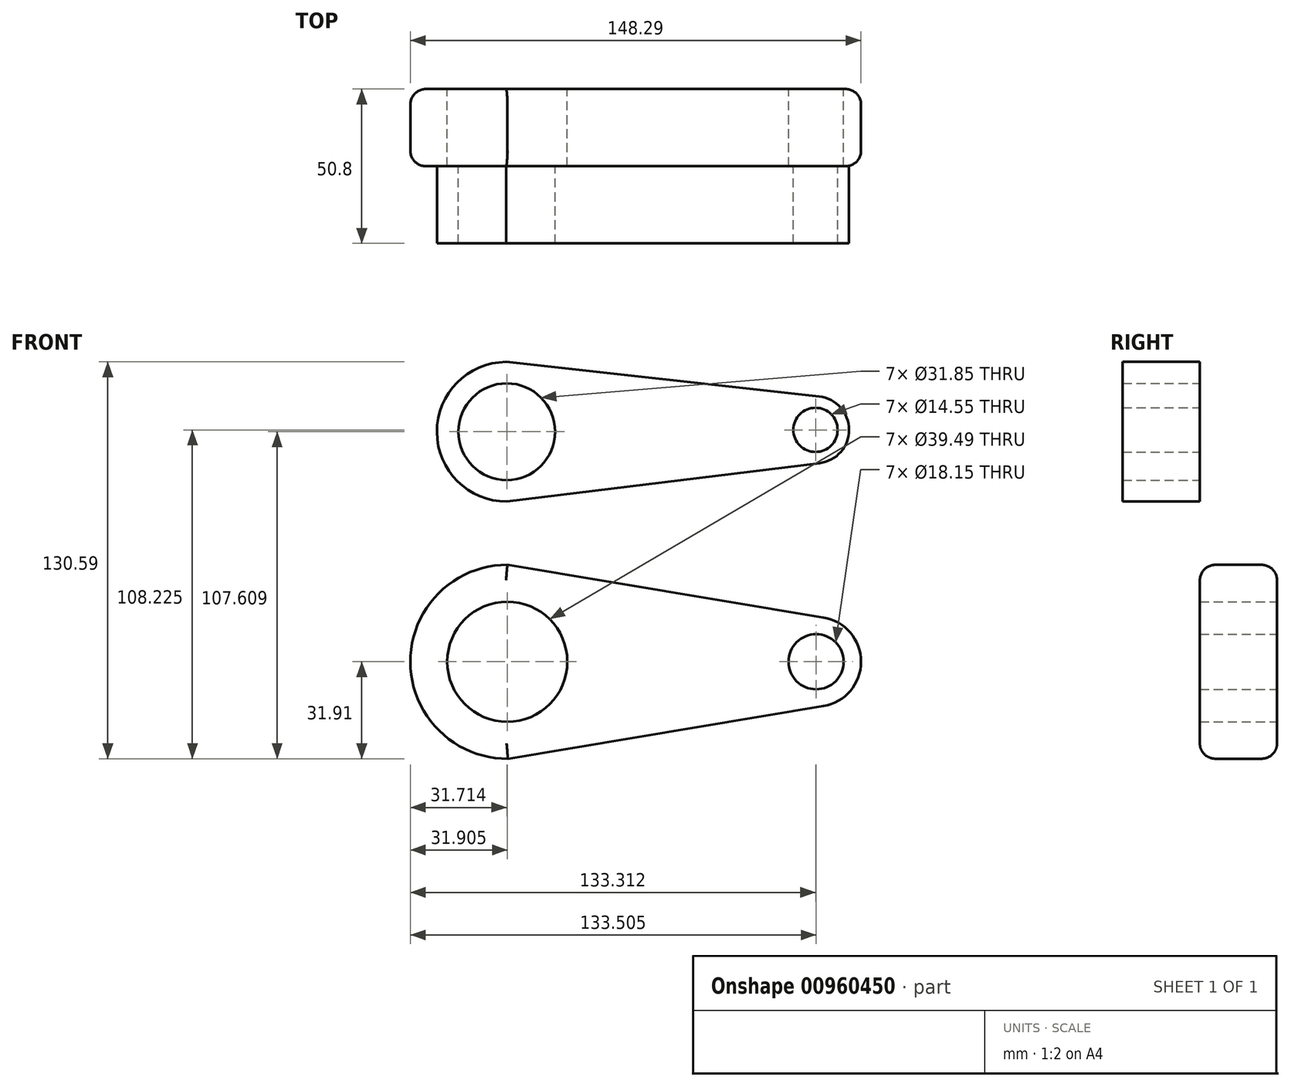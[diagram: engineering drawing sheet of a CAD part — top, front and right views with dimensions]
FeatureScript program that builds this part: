
annotation { "Feature Type Name" : "Feature", "Feature Type Description" : "" }
export const myFeature = defineFeature(function(context is Context, id is Id, definition is map)
    precondition{}
    {
        {
            var Q0;
            Q0=qCreatedBy(makeId("Front.planeOp"),FACE);
            var sketch = newSketch(context, id + "F0", { "sketchPlane" : qUnion([Q0])});
            skArc(sketch, "E0", {"start": v(-52.15, 31.9) * mm, "mid": v(-83.64, -5.16) * mm, "end": v(-41.98, -30.24) * mm});
            skArc(sketch, "E1", {"start": v(51.88, -14.58) * mm, "mid": v(64.23, 0) * mm, "end": v(51.87, 14.58) * mm});
            skLineSegment(sketch, "E2", {"start": v(-52.15, 31.9) * mm, "end": v(51.87, 14.58) * mm});
            skLineSegment(sketch, "E3", {"start": v(-51.96, -31.9) * mm, "end": v(51.88, -14.58) * mm});
            skCircle(sketch, "E4", {"center": v(-52.15, 0) * mm, "radius": 19.74 * mm});
            skCircle(sketch, "E5", {"center": v(49.45, 0) * mm, "radius": 9.08 * mm});
            skSolve(sketch);
        }
        {
            var Q0;
            {var subQ5=sQuery(id+"F0.wireOp",EDGE,"E1");Q0=makeQuery(id+"F0.imprint","IMPRINT",FACE,{"disambiguationData":[TD([[makeQuery(id+"F0.imprint","IMPRINT",EDGE,{"derivedFrom":subQ5}),1.0]])]});}
            extrude(context, id + "F1", {"entities" : qUnion([Q0]), "depth" : 25.4 * mm, "offsetDistance" : 25.4 * mm});
        }
        {
            var Q0;
            Q0=makeQuery(id+"F1.opExtrude","CAP_EDGE",EDGE,{"disambiguationData":[OSD([sQuery(id+"F0.wireOp",EDGE,"E3")])],"isStart":false});
            var Q1;
            Q1=makeQuery(id+"F1.opExtrude","CAP_EDGE",EDGE,{"disambiguationData":[OSD([sQuery(id+"F0.wireOp",EDGE,"E3")])],"isStart":true});
            var Q2;
            Q2=makeQuery(id+"F1.opExtrude","CAP_EDGE",EDGE,{"disambiguationData":[OSD([sQuery(id+"F0.wireOp",EDGE,"E0")])],"isStart":false});
            var Q3;
            Q3=makeQuery(id+"F1.opExtrude","CAP_EDGE",EDGE,{"disambiguationData":[OSD([sQuery(id+"F0.wireOp",EDGE,"E0")])],"isStart":true});
            fillet(context, id + "F2", {"entities" : qUnion([Q0, Q1, Q2, Q3]), "radius" : 5.08 * mm, "tangentPropagation" : true, "allowEdgeOverflow" : false});
        }
        {
            var Q0;
            Q0=makeQuery(id+"F1.opExtrude","CAP_FACE",FACE,{"disambiguationData":[OSD([sQuery(id+"F0.wireOp",EDGE,"E0"),sQuery(id+"F0.wireOp",EDGE,"E1"),sQuery(id+"F0.wireOp",EDGE,"E2"),sQuery(id+"F0.wireOp",EDGE,"E3"),sQuery(id+"F0.wireOp",EDGE,"E4"),sQuery(id+"F0.wireOp",EDGE,"E5")])],"isStart":false});
            var sketch = newSketch(context, id + "F3", { "sketchPlane" : qUnion([Q0])});
            skArc(sketch, "E6", {"start": v(-47.1, 98.07) * mm, "mid": v(-75.32, 75.54) * mm, "end": v(-46.79, 53.4) * mm});
            skArc(sketch, "E7", {"start": v(50.6, 65.36) * mm, "mid": v(60.29, 76.38) * mm, "end": v(50.46, 87.28) * mm});
            skLineSegment(sketch, "E8", {"start": v(-52.58, 98.68) * mm, "end": v(50.46, 87.28) * mm});
            skLineSegment(sketch, "E9", {"start": v(-52.35, 52.72) * mm, "end": v(50.6, 65.36) * mm});
            skCircle(sketch, "E10", {"center": v(-52.35, 75.7) * mm, "radius": 15.93 * mm});
            skCircle(sketch, "E11", {"center": v(49.25, 76.32) * mm, "radius": 7.28 * mm});
            skSolve(sketch);
        }
        {
            var Q0;
            {var subQ0=sQuery(id+"F3.wireOp",EDGE,"E8");var subQ1=sQuery(id+"F3.wireOp",EDGE,"E6");var subQ2=makeQuery(id+"F3.imprint","INTERSECT",VERTEX,{"disambiguationData":[OD(0.0)],"derivedFrom":[subQ1,subQ0]});Q0=makeQuery(id+"F3.imprint","IMPRINT",FACE,{"disambiguationData":[TD([[makeQuery(id+"F3.imprint","IMPRINT",EDGE,{"disambiguationData":[TD([[subQ2,-1.0]])],"derivedFrom":subQ1}),1.0]])]});}
            var Q1;
            {var subQ0=sQuery(id+"F3.wireOp",EDGE,"E9");var subQ1=sQuery(id+"F3.wireOp",EDGE,"E6");var subQ2=makeQuery(id+"F3.imprint","INTERSECT",VERTEX,{"disambiguationData":[OD(0.0)],"derivedFrom":[subQ1,subQ0]});Q1=makeQuery(id+"F3.imprint","IMPRINT",FACE,{"disambiguationData":[TD([[makeQuery(id+"F3.imprint","IMPRINT",EDGE,{"disambiguationData":[TD([[subQ2,1.0]])],"derivedFrom":subQ1}),1.0]])]});}
            var Q2;
            {var subQ3=sQuery(id+"F3.wireOp",EDGE,"E7");Q2=makeQuery(id+"F3.imprint","IMPRINT",FACE,{"disambiguationData":[TD([[makeQuery(id+"F3.imprint","IMPRINT",EDGE,{"derivedFrom":subQ3}),1.0]])]});}
            extrude(context, id + "F4", {"entities" : qUnion([Q0, Q1, Q2]), "depth" : 25.4 * mm, "offsetDistance" : 25.4 * mm});
        }
    });
